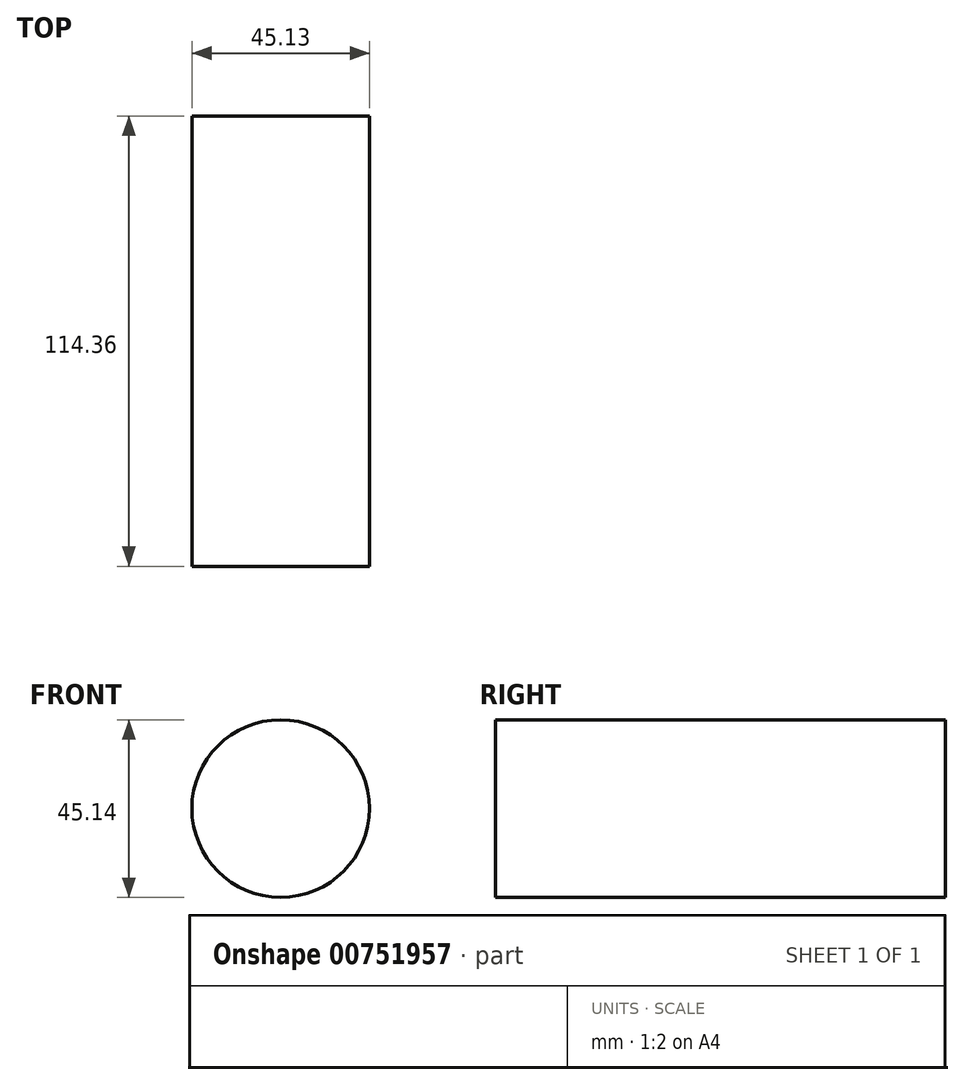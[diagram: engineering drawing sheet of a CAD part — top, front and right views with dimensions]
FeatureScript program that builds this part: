
annotation { "Feature Type Name" : "Feature", "Feature Type Description" : "" }
export const myFeature = defineFeature(function(context is Context, id is Id, definition is map)
    precondition{}
    {
        {
            var Q0;
            Q0=qCreatedBy(makeId("Front.planeOp"),FACE);
            var sketch = newSketch(context, id + "F0", { "sketchPlane" : qUnion([Q0])});
            skCircle(sketch, "E0", {"center": v(25.57, 0) * mm, "radius": 22.57 * mm});
            skSolve(sketch);
        }
        {
            var Q0;
            Q0=makeQuery(id+"F0.imprint","IMPRINT",FACE,{"disambiguationData":[TD([[makeQuery(id+"F0.imprint","IMPRINT",EDGE,{"derivedFrom":sQuery(id+"F0.wireOp",EDGE,"E0")}),1.0]])]});
            extrude(context, id + "F1", {"entities" : qUnion([Q0]), "endBound" : BoundingType.SYMMETRIC, "depth" : 114.37 * mm, "offsetDistance" : 25 * mm});
        }
    });
